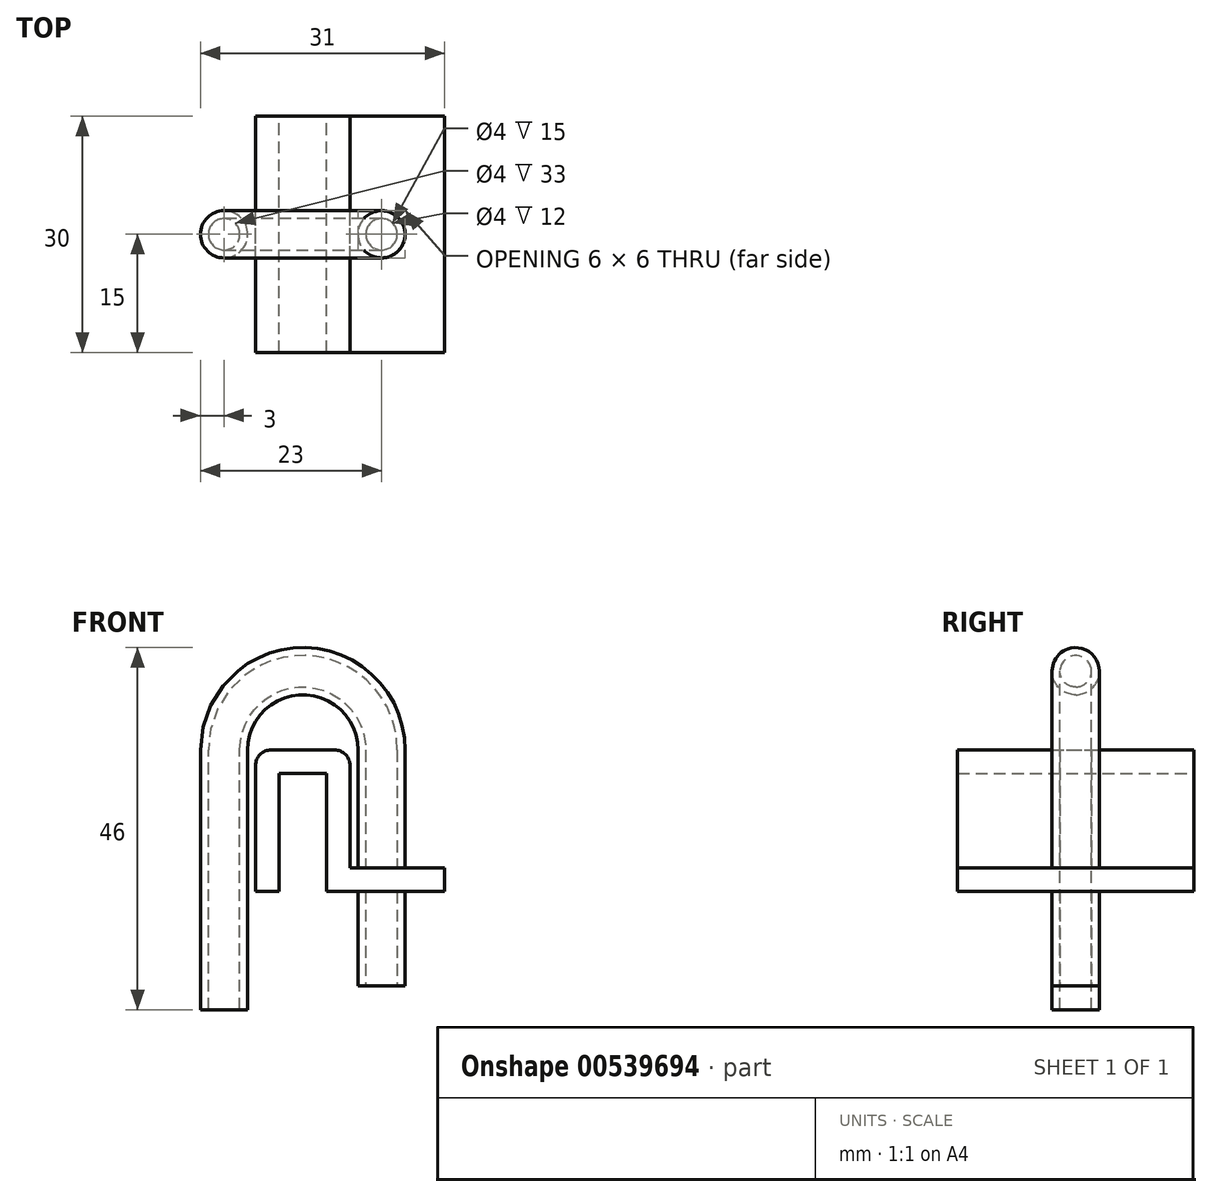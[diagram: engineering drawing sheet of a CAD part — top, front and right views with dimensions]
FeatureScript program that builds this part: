
annotation { "Feature Type Name" : "Feature", "Feature Type Description" : "" }
export const myFeature = defineFeature(function(context is Context, id is Id, definition is map)
    precondition{}
    {
        {
            var Q0;
            Q0=qCreatedBy(makeId("Front.planeOp"),FACE);
            var sketch = newSketch(context, id + "F0", { "sketchPlane" : qUnion([Q0])});
            skLineSegment(sketch, "E0", {"start": v(-3, 30) * mm, "end": v(-3, 15) * mm});
            skLineSegment(sketch, "E1", {"start": v(-3, 30) * mm, "end": v(3, 30) * mm});
            skLineSegment(sketch, "E2", {"start": v(3, 30) * mm, "end": v(3, 15) * mm});
            skLineSegment(sketch, "E3", {"start": v(3, 15) * mm, "end": v(18, 15) * mm});
            skLineSegment(sketch, "E4.0", {"start": v(6, 18) * mm, "end": v(18, 18) * mm});
            skLineSegment(sketch, "E4.1", {"start": v(6, 33) * mm, "end": v(6, 18) * mm});
            skLineSegment(sketch, "E4.2", {"start": v(-6, 33) * mm, "end": v(6, 33) * mm});
            skLineSegment(sketch, "E4.3", {"start": v(-6, 33) * mm, "end": v(-6, 15) * mm});
            skLineSegment(sketch, "E5", {"start": v(-6, 15) * mm, "end": v(-3, 15) * mm});
            skLineSegment(sketch, "E6", {"start": v(18, 18) * mm, "end": v(18, 15) * mm});
            skSolve(sketch);
        }
        {
            var Q0;
            Q0=qSketchRegion(id+"F0",true);
            extrude(context, id + "F1", {"entities" : qUnion([Q0]), "endBound" : BoundingType.SYMMETRIC, "depth" : 30 * mm, "offsetDistance" : 25 * mm});
        }
        {
            var Q0;
            Q0=makeQuery(id+"F1.opExtrude","SWEPT_EDGE",EDGE,{"disambiguationData":[OSD([sQuery(id+"F0.wireOp",EDGE,"E4.1"),sQuery(id+"F0.wireOp",EDGE,"E4.2")])]});
            fillet(context, id + "F2", {"entities" : qUnion([Q0]), "radius" : 2 * mm, "tangentPropagation" : true, "allowEdgeOverflow" : false});
        }
        {
            var Q0;
            Q0=makeQuery(id+"F1.opExtrude","SWEPT_EDGE",EDGE,{"disambiguationData":[OSD([sQuery(id+"F0.wireOp",EDGE,"E4.2"),sQuery(id+"F0.wireOp",EDGE,"E4.3")])]});
            fillet(context, id + "F3", {"entities" : qUnion([Q0]), "radius" : 2 * mm, "tangentPropagation" : true, "allowEdgeOverflow" : false});
        }
        {
            var Q0;
            Q0=qCreatedBy(makeId("Front.planeOp"),FACE);
            var sketch = newSketch(context, id + "F4", { "sketchPlane" : qUnion([Q0])});
            skLineSegment(sketch, "E7", {"start": v(-10, 0) * mm, "end": v(-10, 33) * mm});
            skArc(sketch, "E8", {"start": v(10, 33) * mm, "mid": v(0, 43) * mm, "end": v(-10, 33) * mm});
            skLineSegment(sketch, "E9", {"start": v(10, 33) * mm, "end": v(10, 3) * mm});
            skSolve(sketch);
        }
        {
            var Q0;
            Q0=qCreatedBy(makeId("Top.planeOp"),FACE);
            var sketch = newSketch(context, id + "F5", { "sketchPlane" : qUnion([Q0])});
            skCircle(sketch, "E10", {"center": v(-10, 0) * mm, "radius": 3 * mm});
            skCircle(sketch, "E11.0", {"center": v(-10, 0) * mm, "radius": 2 * mm});
            skSolve(sketch);
        }
        {
            var Q0;
            Q0=makeQuery(id+"F5.imprint","IMPRINT",FACE,{"disambiguationData":[TD([[makeQuery(id+"F5.imprint","IMPRINT",EDGE,{"derivedFrom":sQuery(id+"F5.wireOp",EDGE,"E10")}),1.0]])]});
            var Q1;
            Q1 = qConstructionFilter(qBodyType(qCreatedBy(id + "F4" ,EDGE), BodyType.WIRE), ConstructionObject.NO);
            sweep(context, id + "F6", {"operationType" : NewBodyOperationType.ADD, "profiles" : qUnion([Q0]), "path" : qUnion([Q1])});
        }
    });
